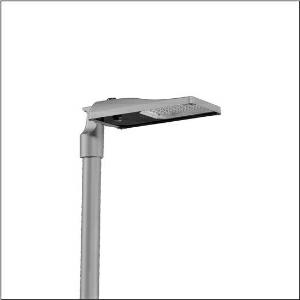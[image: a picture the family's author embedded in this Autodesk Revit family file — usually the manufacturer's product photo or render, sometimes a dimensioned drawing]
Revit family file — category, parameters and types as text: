
# Revit family: streetlight_sl_31_mini___st1_0a_5xh6d71t08ha_56cc
name_source: partatom
category: Lighting Fixtures
units: mm (PartAtom-declared; Revit-internal decimal feet)

## family parameters
Cut with Voids When Loaded = No
Host = Face
Light Source = No
Part Type = Normal
Room Calculation Point = No
Round Connector Dimension = Use Diameter
Shared = No

## types (1)
- --- (1 x LED, 7620 lm, 68.3 W, 2200K)
    Apparent Load = 68 VA
    CIE Flux Codes = 37 72 97 100 100
    Color Rendering = 70
    Color Temperature = 2200K
    Default Elevation = 1800 mm
    Description = Streetlight SL 31 mini D4i, Desk-Remote mast luminaire for post-top, side-entry; light control with lens of PMMA; light distribution: ST1.0a, direct asymmetric distribution, for standard-compliant lighting for roads and squares; LED: luminous flux: 7.620lm, light colour: 722, colour temperature: 2200K; luminous efficacy: 111,6lm/W; control: pre-setting: logarithmic dimming characteristic, flexible luminous flux parameterisation, time-dependent luminous flux control, constant luminous flux control, power reduction, intelligent temperature release in ECG and LED module, overheat protection; luminaire housing, of diecast aluminium, Siteco® metallic grey (DB 702S), corrosivity category C5 high according to DIN EN ISO 12944; cover of toughened safety glass, transparent, opened without tools; mast flange of diecast aluminium, Siteco® metallic grey (DB 702S), spigot size: 76/60mm, mast flange included unmounted; with cable H07RN-F 2x 1.5mm², cable length: 8,5m, connection cable pre-assembled; mains connection: 220..240V, AC, 50/60Hz; power consumption (at start of service life): 68,3W / (at end of service life): 74,5W / (with reduced operation 50%): 29,2W; protection rating (complete): IP66; insulation class (complete): insulation class II (safety insulation); impact resistance: IK09; certification: CE, ENEC, ENEC+, VDE, UKCA, ZD4i; permissible operating ambient temperature for outdoor applications: -40..+50°C; packaging unit: 1 piece

Light Distribution: ST1.0a
    Height = 76 mm
    Lamp = 1 x LED
    Lamp Light Flux = 7620 lm
    Lamp Power = 68.3 W
    Lamp count = 1
    Length = 547 mm
    Luminous efficacy = 112 lm/W
    Manufacturer = Siteco
    ModVariant = No
    Model = 5XH6D71T08HA
    Number of Poles = 1
    OnlyDefault = Yes
    Power Factor = 1
    Product Name = Streetlight SL 31 mini | ST1.0a
    Product group = mast luminaire | pylon top
    ProductGroupID = 6100
    Protection Class = Protection class II
    Protection Degree = IP 66
    RLX_Detail_Level = 1
    RLX_Emergency_Light_Flux = 0 lm
    RLX_Emergency_Type = 0
    RLX_Emergency_Type_DB = No
    RlxData = <blob elided: 24301 chars, md5=8f377020>
    Socket = socket
    Standby Power = 0 W
    System Light Flux = 7620 lm
    System Power = 68 W
    Type Comments = factory setting: luminous flux: 100 % | dim-lin: 254 | 692 mA
    Type Image = l_1300332.jpg
    URL = http://relux.com
    VarID = @adj_001869
    Voltage = 0 V
    Weight = 0.00 kg
    Width = 265 mm

## geometry (parser evidence)
native form markers: Blend x4, Sweep x11
no freeform markers — native parametric forms only
